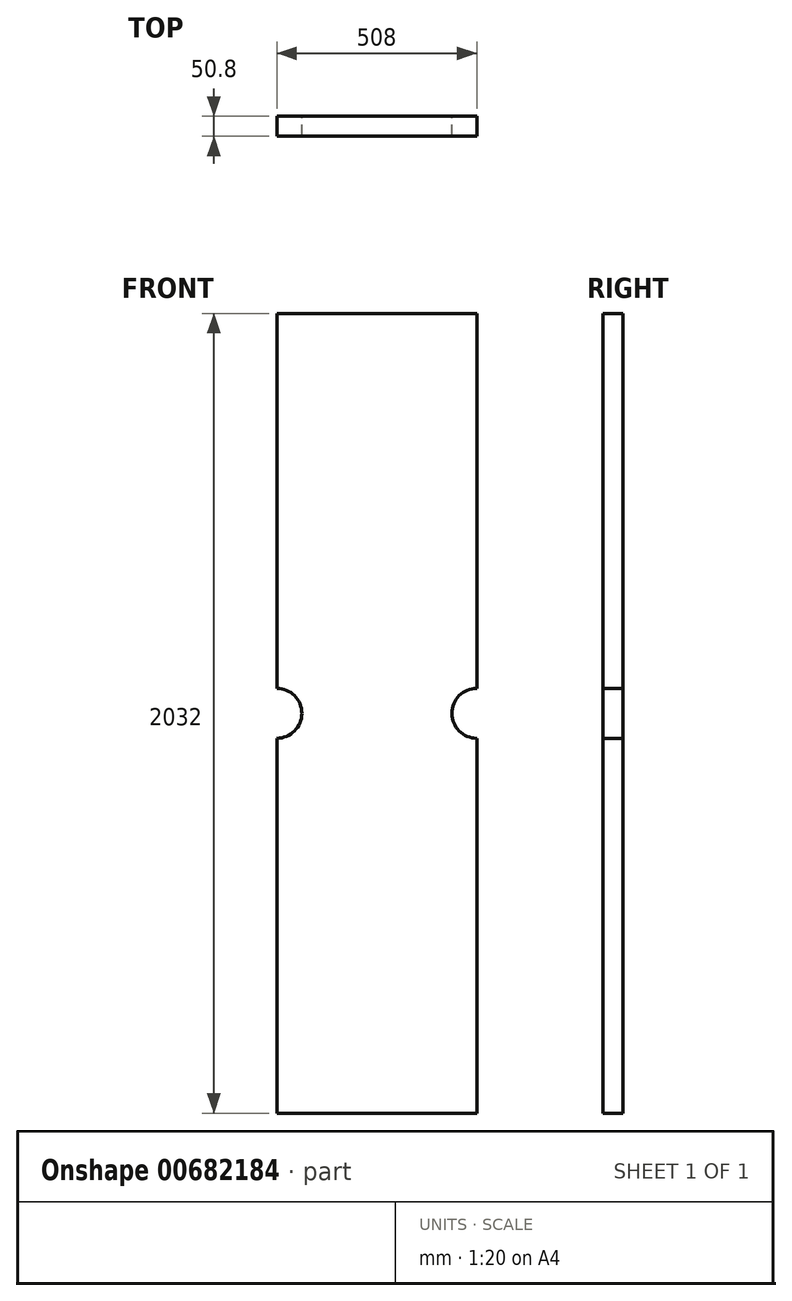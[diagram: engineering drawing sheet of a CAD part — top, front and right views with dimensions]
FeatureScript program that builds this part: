
annotation { "Feature Type Name" : "Feature", "Feature Type Description" : "" }
export const myFeature = defineFeature(function(context is Context, id is Id, definition is map)
    precondition{}
    {
        {
            var Q0;
            Q0=qCreatedBy(makeId("Front.planeOp"),FACE);
            var sketch = newSketch(context, id + "F0", { "sketchPlane" : qUnion([Q0])});
            skLineSegment(sketch, "E0.bottom", {"start": v(-254, 1016) * mm, "end": v(254, 1016) * mm});
            skLineSegment(sketch, "E0.top", {"start": v(-254, -1016) * mm, "end": v(254, -1016) * mm});
            skLineSegment(sketch, "E0.left", {"start": v(-254, 1016) * mm, "end": v(-254, -1016) * mm});
            skLineSegment(sketch, "E0.right", {"start": v(254, 1016) * mm, "end": v(254, -1016) * mm});
            skPoint(sketch, "E0.middle", {"position": v(0, 0) * mm});
            skArc(sketch, "E1", {"start": v(-254, 63.5) * mm, "mid": v(-190.5, 0) * mm, "end": v(-254, -63.5) * mm});
            skLineSegment(sketch, "E2", {"start": v(0, 1016) * mm, "end": v(0, -1016) * mm, "construction": true});
            skArc(sketch, "E3.MirrorCS", {"start": v(254, 63.5) * mm, "mid": v(190.5, 0) * mm, "end": v(254, -63.5) * mm});
            skSolve(sketch);
        }
        {
            var Q0;
            {var subQ3=sQuery(id+"F0.wireOp",EDGE,"E0.bottom");Q0=makeQuery(id+"F0.imprint","IMPRINT",FACE,{"disambiguationData":[TD([[makeQuery(id+"F0.imprint","IMPRINT",EDGE,{"derivedFrom":subQ3}),-1.0]])]});}
            extrude(context, id + "F1", {"entities" : qUnion([Q0]), "depth" : 50.8 * mm, "offsetDistance" : 25.4 * mm});
        }
    });
